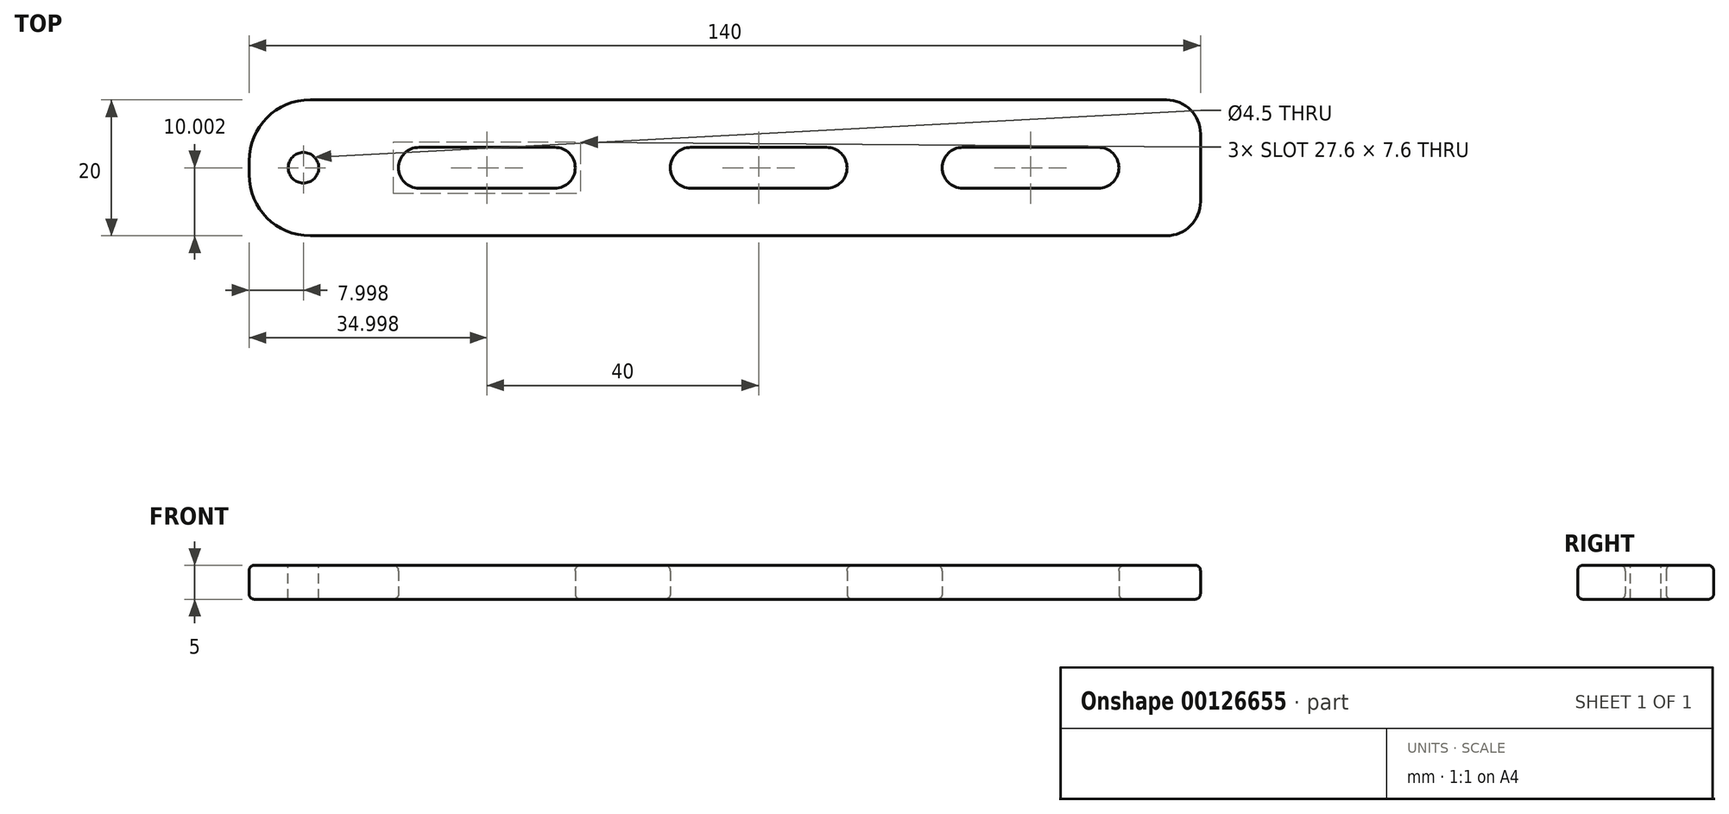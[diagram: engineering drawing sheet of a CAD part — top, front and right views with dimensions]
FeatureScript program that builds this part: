
annotation { "Feature Type Name" : "Feature", "Feature Type Description" : "" }
export const myFeature = defineFeature(function(context is Context, id is Id, definition is map)
    precondition{}
    {
        {
            var Q0;
            Q0=qCreatedBy(makeId("Top.planeOp"),FACE);
            var sketch = newSketch(context, id + "F0", { "sketchPlane" : qUnion([Q0])});
            skLineSegment(sketch, "E0.bottom", {"start": v(-75.85, 35.27) * mm, "end": v(64.15, 35.27) * mm});
            skLineSegment(sketch, "E0.top", {"start": v(-75.85, 15.27) * mm, "end": v(64.15, 15.27) * mm});
            skLineSegment(sketch, "E0.left", {"start": v(-75.85, 35.27) * mm, "end": v(-75.85, 15.27) * mm});
            skLineSegment(sketch, "E0.right", {"start": v(64.15, 35.27) * mm, "end": v(64.15, 15.27) * mm});
            skLineSegment(sketch, "E1", {"start": v(64.15, 25.27) * mm, "end": v(-75.85, 25.27) * mm, "construction": true});
            skCircle(sketch, "E2", {"center": v(-50.85, 25.27) * mm, "radius": 3 * mm});
            skCircle(sketch, "E3.1.0.0", {"center": v(-30.85, 25.27) * mm, "radius": 3 * mm});
            skCircle(sketch, "E3.2.0.0", {"center": v(-10.85, 25.27) * mm, "radius": 3 * mm});
            skCircle(sketch, "E3.3.0.0", {"center": v(9.15, 25.27) * mm, "radius": 3 * mm});
            skCircle(sketch, "E3.4.0.0", {"center": v(29.15, 25.27) * mm, "radius": 3 * mm});
            skCircle(sketch, "E3.5.0.0", {"center": v(49.15, 25.27) * mm, "radius": 3 * mm});
            skLineSegment(sketch, "E3.direction1", {"start": v(-50.85, 25.27) * mm, "end": v(-30.85, 25.27) * mm, "construction": true});
            skLineSegment(sketch, "E4", {"start": v(69.15, 28.27) * mm, "end": v(-50.85, 28.27) * mm});
            skLineSegment(sketch, "E5", {"start": v(-50.85, 22.27) * mm, "end": v(69.15, 22.27) * mm});
            skSolve(sketch);
        }
        {
            var Q0;
            {var subQ6=sQuery(id+"F0.wireOp",EDGE,"E0.bottom");Q0=makeQuery(id+"F0.imprint","IMPRINT",FACE,{"disambiguationData":[TD([[makeQuery(id+"F0.imprint","IMPRINT",EDGE,{"derivedFrom":subQ6}),-1.0]])]});}
            var Q1;
            {var subQ0=sQuery(id+"F0.wireOp",EDGE,"E4");var subQ1=sQuery(id+"F0.wireOp",EDGE,"E0.right");var subQ2=makeQuery(id+"F0.imprint","INTERSECT",VERTEX,{"derivedFrom":[subQ1,subQ0]});Q1=makeQuery(id+"F0.imprint","IMPRINT",FACE,{"disambiguationData":[TD([[makeQuery(id+"F0.imprint","IMPRINT",EDGE,{"disambiguationData":[TD([[subQ2,-1.0]])],"derivedFrom":subQ1}),-1.0]])]});}
            var Q2;
            {var subQ0=sQuery(id+"F0.wireOp",EDGE,"E4");var subQ1=sQuery(id+"F0.wireOp",EDGE,"E3.3.0.0");var subQ2=makeQuery(id+"F0.imprint","INTERSECT",VERTEX,{"derivedFrom":[subQ1,subQ0]});Q2=makeQuery(id+"F0.imprint","IMPRINT",FACE,{"disambiguationData":[TD([[makeQuery(id+"F0.imprint","IMPRINT",EDGE,{"disambiguationData":[TD([[subQ2,1.0]])],"derivedFrom":subQ1}),-1.0]])]});}
            var Q3;
            {var subQ0=sQuery(id+"F0.wireOp",EDGE,"E4");var subQ1=sQuery(id+"F0.wireOp",EDGE,"E3.1.0.0");var subQ2=makeQuery(id+"F0.imprint","INTERSECT",VERTEX,{"derivedFrom":[subQ1,subQ0]});Q3=makeQuery(id+"F0.imprint","IMPRINT",FACE,{"disambiguationData":[TD([[makeQuery(id+"F0.imprint","IMPRINT",EDGE,{"disambiguationData":[TD([[subQ2,1.0]])],"derivedFrom":subQ1}),-1.0]])]});}
            extrude(context, id + "F1", {"entities" : qUnion([Q0, Q1, Q2, Q3]), "depth" : 5 * mm});
        }
        {
            var Q0;
            Q0=makeQuery(id+"F1.opExtrude","SWEPT_EDGE",EDGE,{"disambiguationData":[OSD([sQuery(id+"F0.wireOp",EDGE,"E0.bottom"),sQuery(id+"F0.wireOp",EDGE,"E0.left")])]});
            var Q1;
            Q1=makeQuery(id+"F1.opExtrude","SWEPT_EDGE",EDGE,{"disambiguationData":[OSD([sQuery(id+"F0.wireOp",EDGE,"E0.top"),sQuery(id+"F0.wireOp",EDGE,"E0.left")])]});
            fillet(context, id + "F2", {"entities" : qUnion([Q0, Q1]), "radius" : 9 * mm, "tangentPropagation" : true, "allowEdgeOverflow" : false});
        }
        {
            var Q0;
            Q0=makeQuery(id+"F1.opExtrude","SWEPT_EDGE",EDGE,{"disambiguationData":[OSD([sQuery(id+"F0.wireOp",EDGE,"E0.top"),sQuery(id+"F0.wireOp",EDGE,"E0.right")])]});
            var Q1;
            Q1=makeQuery(id+"F1.opExtrude","SWEPT_EDGE",EDGE,{"disambiguationData":[OSD([sQuery(id+"F0.wireOp",EDGE,"E0.bottom"),sQuery(id+"F0.wireOp",EDGE,"E0.right")])]});
            fillet(context, id + "F3", {"entities" : qUnion([Q0, Q1]), "radius" : 5 * mm, "tangentPropagation" : true, "allowEdgeOverflow" : false});
        }
        {
            var Q0;
            Q0=makeQuery(id+"F1.opExtrude","CAP_EDGE",EDGE,{"disambiguationData":[OSD([sQuery(id+"F0.wireOp",EDGE,"E3.2.0.0")])],"isStart":false});
            var Q1;
            Q1=makeQuery(id+"F1.opExtrude","CAP_EDGE",EDGE,{"disambiguationData":[OSD([sQuery(id+"F0.wireOp",EDGE,"E3.4.0.0")])],"isStart":false});
            var Q2;
            Q2=makeQuery(id+"F1.opExtrude","CAP_EDGE",EDGE,{"disambiguationData":[OSD([sQuery(id+"F0.wireOp",EDGE,"E3.6.0.0")])],"isStart":false});
            var Q3;
            Q3=makeQuery(id+"F1.opExtrude","CAP_EDGE",EDGE,{"disambiguationData":[OSD([sQuery(id+"F0.wireOp",EDGE,"E2")])],"isStart":false});
            var Q4;
            Q4=makeQuery(id+"F1.opExtrude","CAP_EDGE",EDGE,{"disambiguationData":[OSD([sQuery(id+"F0.wireOp",EDGE,"E3.6.0.0")])],"isStart":true});
            var Q5;
            Q5=makeQuery(id+"F1.opExtrude","CAP_EDGE",EDGE,{"disambiguationData":[OSD([sQuery(id+"F0.wireOp",EDGE,"E3.4.0.0")])],"isStart":true});
            var Q6;
            Q6=makeQuery(id+"F1.opExtrude","CAP_EDGE",EDGE,{"disambiguationData":[OSD([sQuery(id+"F0.wireOp",EDGE,"E3.2.0.0")])],"isStart":true});
            var Q7;
            Q7=makeQuery(id+"F1.opExtrude","CAP_EDGE",EDGE,{"disambiguationData":[OSD([sQuery(id+"F0.wireOp",EDGE,"E2")])],"isStart":true});
            var Q8;
            Q8=makeQuery(id+"F1.opExtrude","CAP_EDGE",EDGE,{"disambiguationData":[OSD([sQuery(id+"F0.wireOp",EDGE,"E0.top")])],"isStart":false});
            var Q9;
            Q9=makeQuery(id+"F1.opExtrude","CAP_EDGE",EDGE,{"disambiguationData":[OSD([sQuery(id+"F0.wireOp",EDGE,"E0.top")])],"isStart":true});
            fillet(context, id + "F4", {"entities" : qUnion([Q0, Q1, Q2, Q3, Q4, Q5, Q6, Q7, Q8, Q9]), "radius" : 0.8 * mm, "tangentPropagation" : true, "allowEdgeOverflow" : false});
        }
        {
            var Q0;
            Q0=makeQuery(id+"F1.opExtrude","CAP_FACE",FACE,{"disambiguationData":[OSD([sQuery(id+"F0.wireOp",EDGE,"E0.bottom"),sQuery(id+"F0.wireOp",EDGE,"E0.top"),sQuery(id+"F0.wireOp",EDGE,"E0.left"),sQuery(id+"F0.wireOp",EDGE,"E0.right"),sQuery(id+"F0.wireOp",EDGE,"E2"),sQuery(id+"F0.wireOp",EDGE,"E3.1.0.0"),sQuery(id+"F0.wireOp",EDGE,"E3.2.0.0"),sQuery(id+"F0.wireOp",EDGE,"E3.3.0.0"),sQuery(id+"F0.wireOp",EDGE,"E3.4.0.0"),sQuery(id+"F0.wireOp",EDGE,"E3.5.0.0"),sQuery(id+"F0.wireOp",EDGE,"E4"),sQuery(id+"F0.wireOp",EDGE,"E5")])],"isStart":false});
            var sketch = newSketch(context, id + "F5", { "sketchPlane" : qUnion([Q0])});
            skLineSegment(sketch, "E6", {"start": v(-75.85, 25.27) * mm, "end": v(-21.46, 25.27) * mm, "construction": true});
            skPoint(sketch, "E6.endSnap0", {"position": v(-54.65, 25.27) * mm});
            skCircle(sketch, "E7", {"center": v(-67.85, 25.27) * mm, "radius": 2.25 * mm});
            skSolve(sketch);
        }
        {
            var Q0;
            Q0=makeQuery(id+"F5.imprint","IMPRINT",FACE,{"disambiguationData":[TD([[makeQuery(id+"F5.imprint","IMPRINT",EDGE,{"derivedFrom":sQuery(id+"F5.wireOp",EDGE,"E7")}),1.0]])]});
            extrude(context, id + "F6", {"entities" : qUnion([Q0]), "operationType" : NewBodyOperationType.REMOVE, "oppositeDirection" : true, "depth" : 25 * mm});
        }
    });
